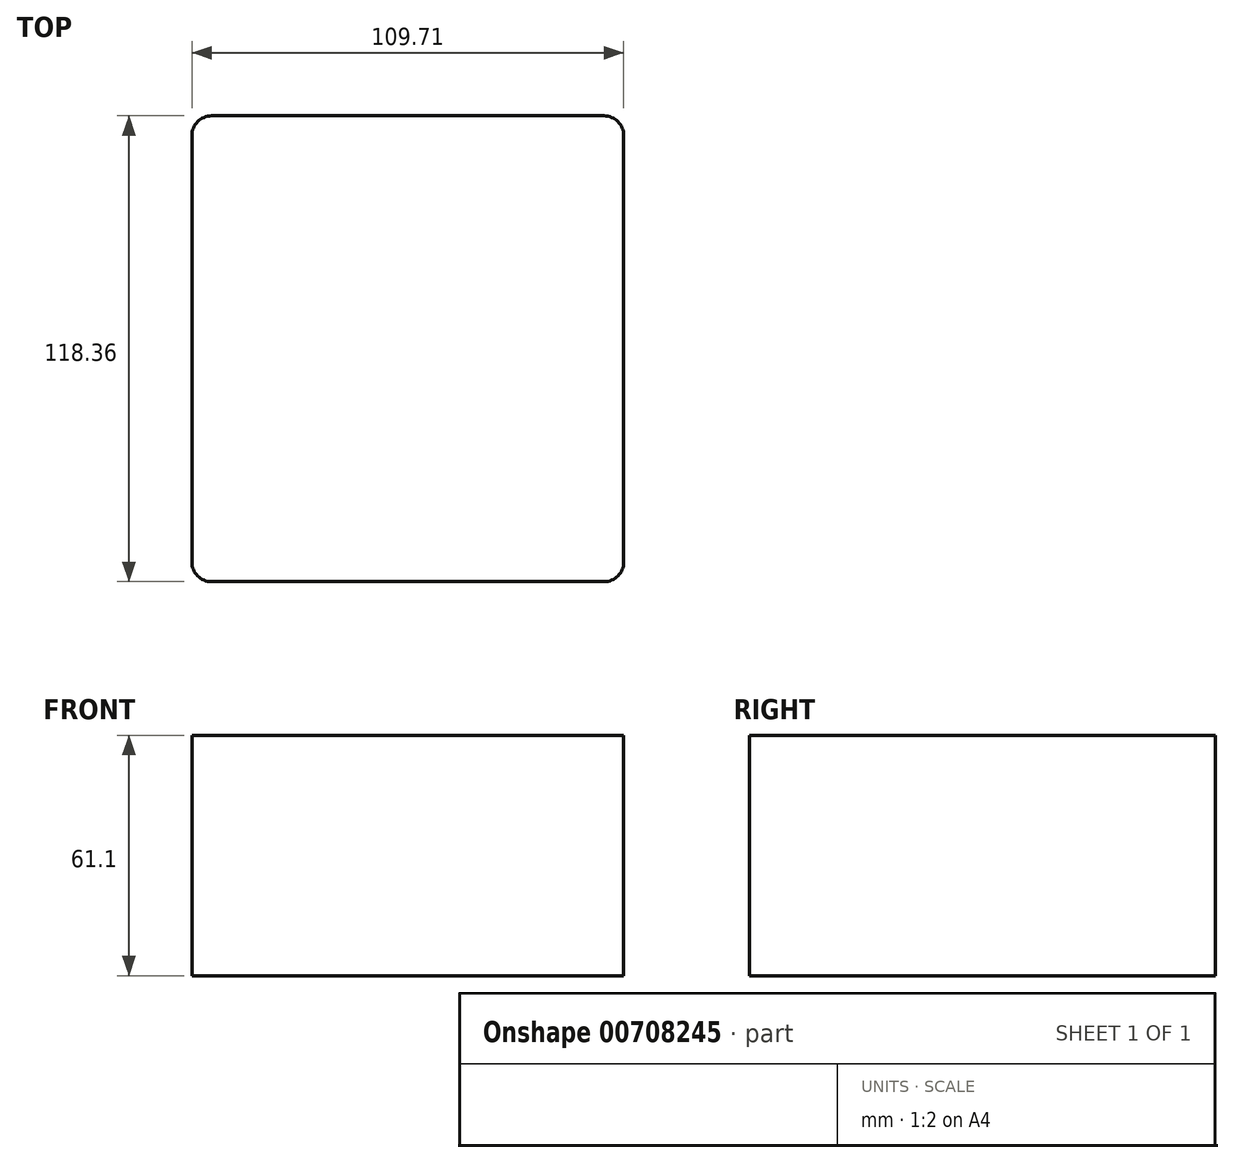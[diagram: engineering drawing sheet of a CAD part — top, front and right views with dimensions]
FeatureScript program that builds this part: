
annotation { "Feature Type Name" : "Feature", "Feature Type Description" : "" }
export const myFeature = defineFeature(function(context is Context, id is Id, definition is map)
    precondition{}
    {
        {
            var Q0;
            Q0=qCreatedBy(makeId("Top.planeOp"),FACE);
            var sketch = newSketch(context, id + "F0", { "sketchPlane" : qUnion([Q0])});
            skLineSegment(sketch, "E0.bottom", {"start": v(44.25, -59.18) * mm, "end": v(-55.46, -59.18) * mm});
            skLineSegment(sketch, "E0.top", {"start": v(44.25, 59.18) * mm, "end": v(-55.46, 59.18) * mm});
            skLineSegment(sketch, "E0.left", {"start": v(49.25, -54.18) * mm, "end": v(49.25, 54.18) * mm});
            skLineSegment(sketch, "E0.right", {"start": v(-60.46, -54.18) * mm, "end": v(-60.46, 54.18) * mm});
            skPoint(sketch, "E0.middle", {"position": v(-5.6, 0) * mm});
            skPoint(sketch, "E1.visualSharp", {"position": v(-60.46, 59.18) * mm});
            skArc(sketch, "E1.filletArc", {"start": v(-55.46, 59.18) * mm, "mid": v(-59, 57.71) * mm, "end": v(-60.46, 54.18) * mm});
            skPoint(sketch, "E2.visualSharp", {"position": v(49.25, 59.18) * mm});
            skArc(sketch, "E2.filletArc", {"start": v(49.25, 54.18) * mm, "mid": v(47.78, 57.71) * mm, "end": v(44.25, 59.18) * mm});
            skPoint(sketch, "E3.visualSharp", {"position": v(49.25, -59.18) * mm});
            skArc(sketch, "E3.filletArc", {"start": v(44.25, -59.18) * mm, "mid": v(47.16, -58.24) * mm, "end": v(48.98, -55.78) * mm});
            skPoint(sketch, "E4.visualSharp", {"position": v(-60.46, -59.18) * mm});
            skArc(sketch, "E4.filletArc", {"start": v(-60.46, -54.18) * mm, "mid": v(-59, -57.71) * mm, "end": v(-55.46, -59.18) * mm});
            skPoint(sketch, "E5.visualSharp", {"position": v(49.25, -54.18) * mm});
            skArc(sketch, "E5.filletArc", {"start": v(48.98, -55.78) * mm, "mid": v(49.18, -54.99) * mm, "end": v(49.25, -54.18) * mm});
            skSolve(sketch);
        }
        {
            var Q0;
            Q0=makeQuery(id+"F0.imprint","IMPRINT",FACE,{"disambiguationData":[TD([[makeQuery(id+"F0.imprint","IMPRINT",EDGE,{"derivedFrom":sQuery(id+"F0.wireOp",EDGE,"E0.bottom")}),-1.0]])]});
            extrude(context, id + "F1", {"entities" : qUnion([Q0]), "depth" : 61.1 * mm, "offsetDistance" : 25 * mm});
        }
    });
